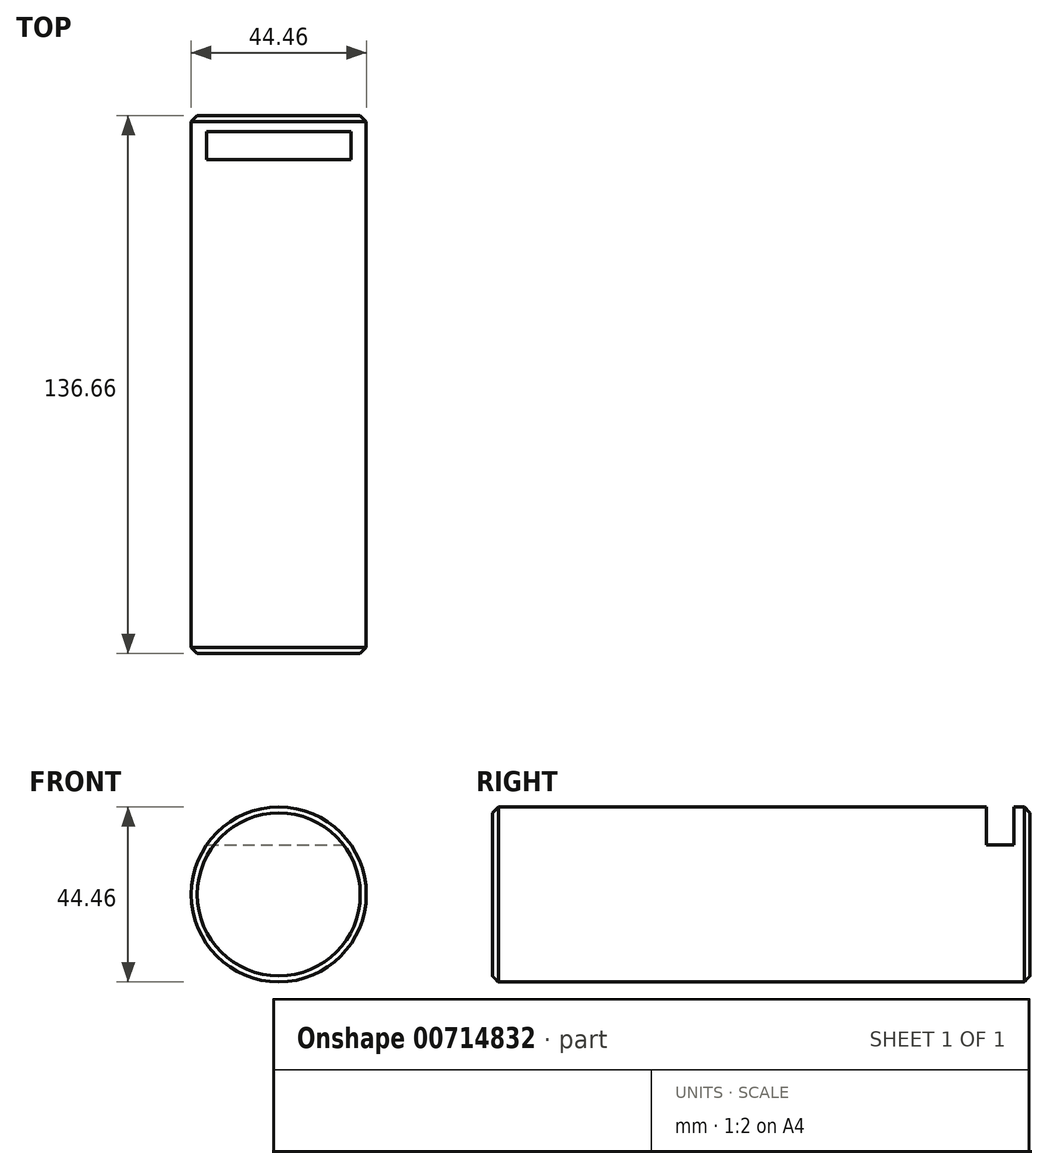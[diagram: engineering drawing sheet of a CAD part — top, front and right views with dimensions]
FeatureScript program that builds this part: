
annotation { "Feature Type Name" : "Feature", "Feature Type Description" : "" }
export const myFeature = defineFeature(function(context is Context, id is Id, definition is map)
    precondition{}
    {
        {
            var Q0;
            Q0=qCreatedBy(makeId("Front.planeOp"),FACE);
            var sketch = newSketch(context, id + "F0", { "sketchPlane" : qUnion([Q0])});
            skCircle(sketch, "E0", {"center": v(0, 0) * mm, "radius": 22.23 * mm});
            skSolve(sketch);
        }
        {
            var Q0;
            Q0 = qSketchRegion(id + "F0", true);
            extrude(context, id + "F1", {"entities" : qUnion([Q0]), "endBound" : BoundingType.SYMMETRIC, "depth" : 136.65 * mm, "offsetDistance" : 25.4 * mm});
        }
        {
            var Q0;
            Q0=makeQuery(id+"F1.opExtrude","CAP_FACE",FACE,{"disambiguationData":[OSD([sQuery(id+"F0.wireOp",EDGE,"E0")])],"isStart":false});
            var Q1;
            Q1=makeQuery(id+"F1.opExtrude","CAP_FACE",FACE,{"disambiguationData":[OSD([sQuery(id+"F0.wireOp",EDGE,"E0")])],"isStart":true});
            chamfer(context, id + "F2", {"entities" : qUnion([Q0, Q1]), "width" : 1.52 * mm, "tangentPropagation" : true});
        }
        {
            var Q0;
            Q0=qCreatedBy(makeId("Right.planeOp"),FACE);
            var sketch = newSketch(context, id + "F3", { "sketchPlane" : qUnion([Q0])});
            skLineSegment(sketch, "E1", {"start": v(-66.8, 22.23) * mm, "end": v(66.8, 22.23) * mm, "construction": true});
            skLineSegment(sketch, "E2.bottom", {"start": v(64.26, 31.88) * mm, "end": v(57.15, 31.88) * mm});
            skLineSegment(sketch, "E2.top", {"start": v(64.26, 12.57) * mm, "end": v(57.15, 12.57) * mm});
            skLineSegment(sketch, "E2.left", {"start": v(64.26, 31.88) * mm, "end": v(64.26, 12.57) * mm});
            skLineSegment(sketch, "E2.right", {"start": v(57.15, 31.88) * mm, "end": v(57.15, 12.57) * mm});
            skPoint(sketch, "E2.middle", {"position": v(60.7, 22.23) * mm});
            skLineSegment(sketch, "E3", {"start": v(0, 102.2) * mm, "end": v(0, -68.3) * mm, "construction": true});
            skSolve(sketch);
        }
        {
            var Q0;
            Q0 = qSketchRegion(id + "F3", true);
            extrude(context, id + "F4", {"entities" : qUnion([Q0]), "operationType" : NewBodyOperationType.REMOVE, "endBound" : BoundingType.SYMMETRIC, "oppositeDirection" : true, "depth" : 50.8 * mm, "offsetDistance" : 25.4 * mm});
        }
    });
